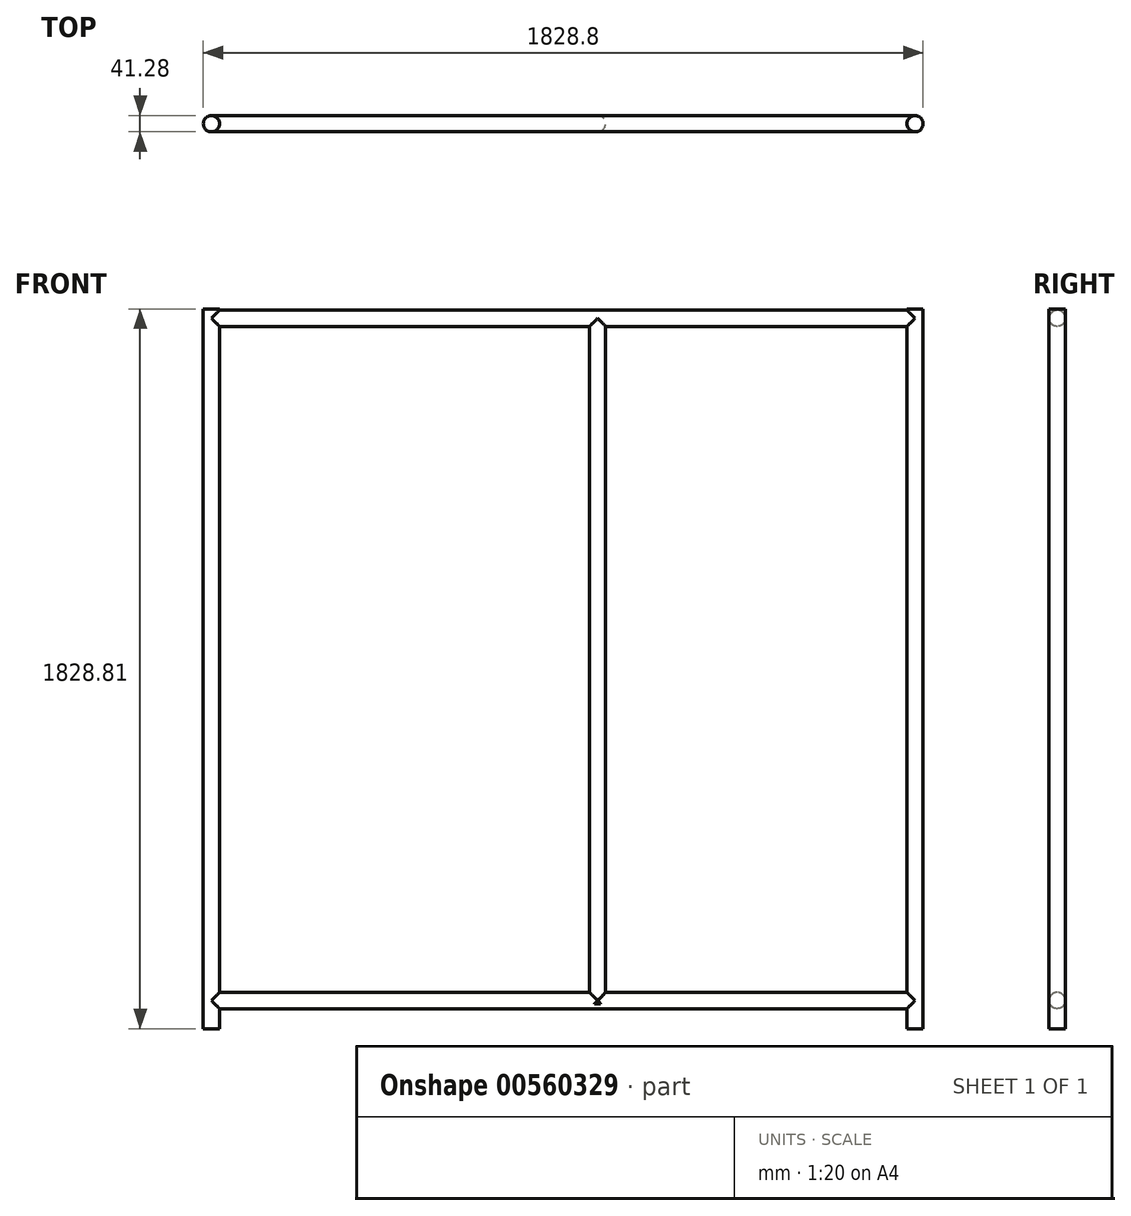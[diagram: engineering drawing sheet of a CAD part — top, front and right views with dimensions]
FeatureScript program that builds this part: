
annotation { "Feature Type Name" : "Feature", "Feature Type Description" : "" }
export const myFeature = defineFeature(function(context is Context, id is Id, definition is map)
    precondition{}
    {
        {
            var Q0;
            Q0=qCreatedBy(makeId("Top.planeOp"),FACE);
            var sketch = newSketch(context, id + "F0", { "sketchPlane" : qUnion([Q0])});
            skCircle(sketch, "E0", {"center": v(0, 0) * mm, "radius": 20.64 * mm});
            skCircle(sketch, "E1", {"center": v(1787.53, 0) * mm, "radius": 20.64 * mm});
            skLineSegment(sketch, "E2", {"start": v(0, 0) * mm, "end": v(1787.53, 0) * mm, "construction": true});
            skSolve(sketch);
        }
        {
            var Q0;
            Q0=makeQuery(id+"F0.imprint","IMPRINT",FACE,{"disambiguationData":[TD([[makeQuery(id+"F0.imprint","IMPRINT",EDGE,{"derivedFrom":sQuery(id+"F0.wireOp",EDGE,"E0")}),1.0]])]});
            var Q1;
            Q1=makeQuery(id+"F0.imprint","IMPRINT",FACE,{"disambiguationData":[TD([[makeQuery(id+"F0.imprint","IMPRINT",EDGE,{"derivedFrom":sQuery(id+"F0.wireOp",EDGE,"E1")}),1.0]])]});
            extrude(context, id + "F1", {"entities" : qUnion([Q0, Q1]), "depth" : 1828.8 * mm + 1 / 101.6 * mm, "offsetDistance" : 25.4 * mm});
        }
        {
            var Q0;
            Q0=qCreatedBy(makeId("Right.planeOp"),FACE);
            var sketch = newSketch(context, id + "F2", { "sketchPlane" : qUnion([Q0])});
            skCircle(sketch, "E3", {"center": v(0, 71.44) * mm, "radius": 20.64 * mm});
            skLineSegment(sketch, "E4", {"start": v(0, 0) * mm, "end": v(0, 2132.66) * mm, "construction": true});
            skCircle(sketch, "E5", {"center": v(0, 1804.99) * mm, "radius": 20.64 * mm});
            skLineSegment(sketch, "E6", {"start": v(72.47, 71.44) * mm, "end": v(-103.35, 71.44) * mm, "construction": true});
            skSolve(sketch);
        }
        {
            var Q0;
            Q0=makeQuery(id+"F2.imprint","IMPRINT",FACE,{"disambiguationData":[TD([[makeQuery(id+"F2.imprint","IMPRINT",EDGE,{"derivedFrom":sQuery(id+"F2.wireOp",EDGE,"E3")}),1.0]])]});
            var Q1;
            Q1=makeQuery(id+"F2.imprint","IMPRINT",FACE,{"disambiguationData":[TD([[makeQuery(id+"F2.imprint","IMPRINT",EDGE,{"derivedFrom":sQuery(id+"F2.wireOp",EDGE,"E5")}),1.0]])]});
            var Q2;
            Q2=makeQuery(id+"F1.opExtrude","SWEPT_BODY",BODY,{"disambiguationData":[OSD([sQuery(id+"F0.wireOp",EDGE,"E1")])]});
            extrude(context, id + "F3", {"entities" : qUnion([Q0, Q1]), "operationType" : NewBodyOperationType.ADD, "endBound" : BoundingType.UP_TO_BODY, "depth" : 184.9 * mm, "endBoundEntityBody" : qUnion([Q2]), "offsetDistance" : 25.4 * mm});
        }
        {
            var Q0;
            Q0=qCreatedBy(makeId("Top.planeOp"),FACE);
            cPlane(context, id + "F4", {"entities" : qUnion([Q0]), "cplaneType" : CPlaneType.OFFSET, "offset" : 50.8 * mm + ((25.4 * mm + 5 / 203.2 * mm) / 2), "width" : 152.4 * mm, "height" : 152.4 * mm});
        }
        {
            var Q0;
            Q0=qCreatedBy(id+"F4.planeOp",FACE);
            var sketch = newSketch(context, id + "F5", { "sketchPlane" : qUnion([Q0])});
            skCircle(sketch, "E7", {"center": v(981.08, 0) * mm, "radius": 20.64 * mm});
            skLineSegment(sketch, "E8", {"start": v(0, 0) * mm, "end": v(1886.44, 0) * mm, "construction": true});
            skSolve(sketch);
        }
        {
            var Q0;
            Q0=makeQuery(id+"F5.imprint","IMPRINT",FACE,{"disambiguationData":[TD([[makeQuery(id+"F5.imprint","IMPRINT",EDGE,{"derivedFrom":sQuery(id+"F5.wireOp",EDGE,"E7")}),1.0]])]});
            var Q1;
            Q1=makeQuery(id+"F3.opExtrude","SWEPT_FACE",FACE,{"disambiguationData":[OSD([sQuery(id+"F2.wireOp",EDGE,"E5")])]});
            extrude(context, id + "F6", {"entities" : qUnion([Q0]), "operationType" : NewBodyOperationType.ADD, "endBound" : BoundingType.UP_TO_SURFACE, "depth" : 25.4 * mm, "endBoundEntityFace" : qUnion([Q1]), "offsetDistance" : 25.4 * mm});
        }
    });
